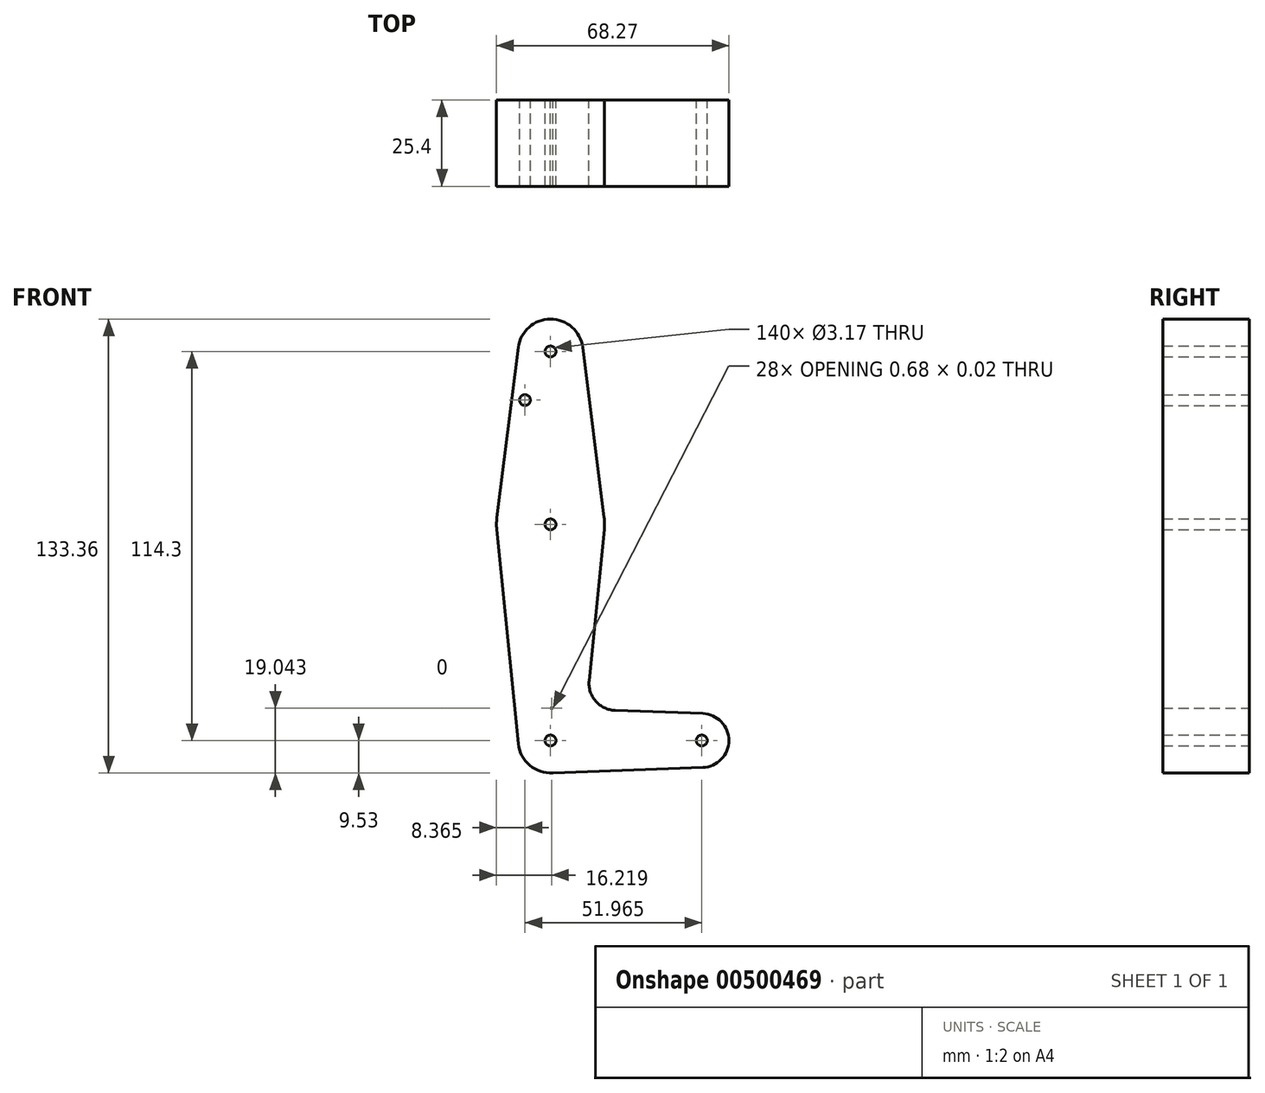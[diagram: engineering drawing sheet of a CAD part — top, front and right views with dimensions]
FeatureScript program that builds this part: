
annotation { "Feature Type Name" : "Feature", "Feature Type Description" : "" }
export const myFeature = defineFeature(function(context is Context, id is Id, definition is map)
    precondition{}
    {
        {
            var Q0;
            Q0=qCreatedBy(makeId("Front.planeOp"),FACE);
            var sketch = newSketch(context, id + "F0", { "sketchPlane" : qUnion([Q0])});
            skLineSegment(sketch, "E0", {"start": v(0, 114.3) * mm, "end": v(0, 0) * mm, "construction": true});
            skLineSegment(sketch, "E1", {"start": v(0, 0) * mm, "end": v(44.45, 0) * mm, "construction": true});
            skCircle(sketch, "E2", {"center": v(0, 114.3) * mm, "radius": 9.53 * mm});
            skCircle(sketch, "E3", {"center": v(0, 63.5) * mm, "radius": 15.88 * mm});
            skCircle(sketch, "E4", {"center": v(0, 0) * mm, "radius": 9.53 * mm});
            skCircle(sketch, "E5", {"center": v(44.45, 0) * mm, "radius": 7.94 * mm});
            skLineSegment(sketch, "E6", {"start": v(-9.45, 115.5) * mm, "end": v(-15.75, 65.48) * mm});
            skLineSegment(sketch, "E7", {"start": v(9.45, 115.5) * mm, "end": v(15.75, 65.48) * mm});
            skLineSegment(sketch, "E8", {"start": v(15.8, 61.91) * mm, "end": v(11.34, 17.59) * mm});
            skLineSegment(sketch, "E9", {"start": v(-15.8, 61.91) * mm, "end": v(-9.48, -0.95) * mm});
            skLineSegment(sketch, "E10", {"start": v(0, 9.53) * mm, "end": v(0.68, 9.5) * mm});
            skLineSegment(sketch, "E11", {"start": v(0, -9.53) * mm, "end": v(44.73, -7.93) * mm});
            skCircle(sketch, "E12", {"center": v(0, 114.3) * mm, "radius": 1.59 * mm});
            skCircle(sketch, "E13", {"center": v(-7.51, 100.03) * mm, "radius": 1.59 * mm});
            skCircle(sketch, "E14", {"center": v(0, 63.5) * mm, "radius": 1.59 * mm});
            skCircle(sketch, "E15", {"center": v(0, 0) * mm, "radius": 1.59 * mm});
            skCircle(sketch, "E16", {"center": v(44.45, 0) * mm, "radius": 1.59 * mm});
            skLineSegment(sketch, "E17.trimOffspring", {"start": v(18.97, 8.85) * mm, "end": v(44.73, 7.93) * mm});
            skLineSegment(sketch, "E18.trimOffspring", {"start": v(9.57, 0) * mm, "end": v(9.48, -0.95) * mm});
            skPoint(sketch, "E19.visualSharp", {"position": v(10.5, 9.15) * mm});
            skArc(sketch, "E19.filletArc", {"start": v(11.34, 17.59) * mm, "mid": v(13.26, 11.57) * mm, "end": v(18.97, 8.85) * mm});
            skSolve(sketch);
        }
        {
            var Q0;
            Q0=qSketchRegion(id+"F0",true);
            extrude(context, id + "F1", {"entities" : qUnion([Q0]), "depth" : 25.4 * mm});
        }
    });
